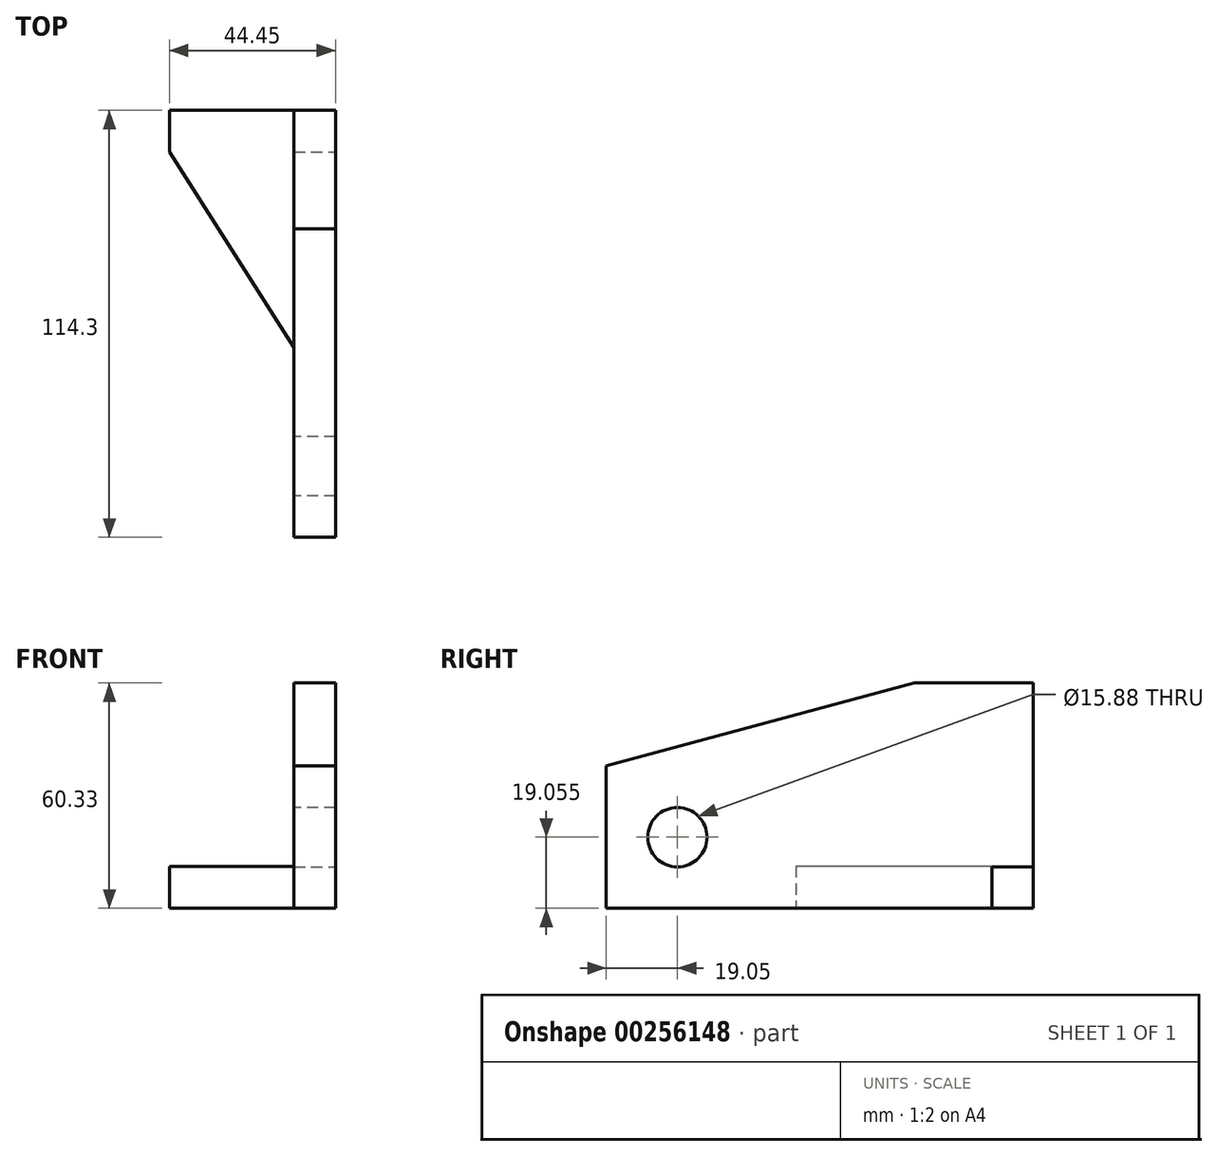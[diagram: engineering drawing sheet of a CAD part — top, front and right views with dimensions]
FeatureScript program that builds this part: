
annotation { "Feature Type Name" : "Feature", "Feature Type Description" : "" }
export const myFeature = defineFeature(function(context is Context, id is Id, definition is map)
    precondition{}
    {
        {
            var Q0;
            Q0=qCreatedBy(makeId("Front.planeOp"),FACE);
            var sketch = newSketch(context, id + "F0", { "sketchPlane" : qUnion([Q0])});
            skLineSegment(sketch, "E0.bottom", {"start": v(-5.09, -11.25) * mm, "end": v(-16.2, -11.25) * mm});
            skLineSegment(sketch, "E0.top", {"start": v(-5.09, 49.08) * mm, "end": v(-16.2, 49.08) * mm});
            skLineSegment(sketch, "E0.left", {"start": v(-5.09, -11.25) * mm, "end": v(-5.09, 49.08) * mm});
            skLineSegment(sketch, "E0.right", {"start": v(-16.2, -11.25) * mm, "end": v(-16.2, 49.08) * mm});
            skLineSegment(sketch, "E1", {"start": v(-16.2, -11.25) * mm, "end": v(-16.2, 39.55) * mm});
            skLineSegment(sketch, "E2", {"start": v(-5.09, -11.25) * mm, "end": v(-49.54, -11.25) * mm});
            skPoint(sketch, "E2.endSnap0", {"position": v(-10.64, -11.25) * mm});
            skLineSegment(sketch, "E3", {"start": v(-49.54, -11.25) * mm, "end": v(-49.54, 10.98) * mm});
            skLineSegment(sketch, "E4", {"start": v(-16.2, 39.55) * mm, "end": v(-33.04, 39.55) * mm});
            skLineSegment(sketch, "E5", {"start": v(-49.54, 10.98) * mm, "end": v(-33.04, 39.55) * mm});
            skPoint(sketch, "E6.end.orphan", {"position": v(-49.54, 39.55) * mm});
            skPoint(sketch, "E7.oppositeSnap0", {"position": v(-49.54, -0.13) * mm});
            skLineSegment(sketch, "E7.bottom", {"start": v(-49.54, -11.25) * mm, "end": v(-5.09, -11.25) * mm});
            skLineSegment(sketch, "E7.top", {"start": v(-49.54, -0.13) * mm, "end": v(-5.09, -0.13) * mm});
            skLineSegment(sketch, "E7.left", {"start": v(-49.54, -11.25) * mm, "end": v(-49.54, -0.13) * mm});
            skLineSegment(sketch, "E7.right", {"start": v(-5.09, -11.25) * mm, "end": v(-5.09, -0.13) * mm});
            skSolve(sketch);
        }
        {
            var Q0;
            {var subQ1=sQuery(id+"F0.wireOp",EDGE,"E3");Q0=makeQuery(id+"F0.imprint","IMPRINT",FACE,{"disambiguationData":[TD([[makeQuery(id+"F0.imprint","IMPRINT",EDGE,{"derivedFrom":subQ1}),-1.0]])]});}
            var Q1;
            {var subQ5=sQuery(id+"F0.wireOp",EDGE,"E7.left");Q1=makeQuery(id+"F0.imprint","IMPRINT",FACE,{"disambiguationData":[TD([[makeQuery(id+"F0.imprint","IMPRINT",EDGE,{"derivedFrom":subQ5}),-1.0]])]});}
            var Q2;
            {var subQ5=sQuery(id+"F0.wireOp",EDGE,"E7.right");Q2=makeQuery(id+"F0.imprint","IMPRINT",FACE,{"disambiguationData":[TD([[makeQuery(id+"F0.imprint","IMPRINT",EDGE,{"derivedFrom":subQ5}),1.0]])]});}
            var Q3;
            Q3=makeQuery(id+"F0.imprint","IMPRINT",FACE,{"disambiguationData":[TD([[makeQuery(id+"F0.imprint","IMPRINT",EDGE,{"derivedFrom":sQuery(id+"F0.wireOp",EDGE,"E0.top")}),1.0]])]});
            extrude(context, id + "F1", {"entities" : qUnion([Q0, Q1, Q2, Q3]), "depth" : 11.1 * mm});
        }
        {
            var Q0;
            Q0=makeQuery(id+"F1.opExtrude","CAP_FACE",FACE,{"disambiguationData":[OSD([sQuery(id+"F0.wireOp",EDGE,"E0.top"),sQuery(id+"F0.wireOp",EDGE,"E0.left"),sQuery(id+"F0.wireOp",EDGE,"E0.right"),sQuery(id+"F0.wireOp",EDGE,"E3"),sQuery(id+"F0.wireOp",EDGE,"E4"),sQuery(id+"F0.wireOp",EDGE,"E5"),sQuery(id+"F0.wireOp",EDGE,"E7.bottom"),sQuery(id+"F0.wireOp",EDGE,"E7.left"),sQuery(id+"F0.wireOp",EDGE,"E7.right")])],"isStart":false});
            var sketch = newSketch(context, id + "F2", { "sketchPlane" : qUnion([Q0])});
            skLineSegment(sketch, "E8", {"start": v(-16.2, 49.08) * mm, "end": v(-16.2, -11.25) * mm});
            skLineSegment(sketch, "E9", {"start": v(-16.2, 49.08) * mm, "end": v(-5.09, 49.08) * mm});
            skLineSegment(sketch, "E10", {"start": v(-5.09, 49.08) * mm, "end": v(-5.09, -11.25) * mm});
            skLineSegment(sketch, "E11", {"start": v(-16.2, -11.25) * mm, "end": v(-5.09, -11.25) * mm});
            skSolve(sketch);
        }
        {
            var Q0;
            Q0 = qSketchRegion(id + "F2", true);
            extrude(context, id + "F3", {"entities" : qUnion([Q0]), "operationType" : NewBodyOperationType.ADD, "depth" : 103.19 * mm});
        }
        {
            var Q0;
            Q0=makeQuery(id+"F3.boolean.opBoolean","MERGE",FACE,{"derivedFrom":[makeQuery(id+"F1.opExtrude","SWEPT_FACE",FACE,{"disambiguationData":[OSD([sQuery(id+"F0.wireOp",EDGE,"E0.right")])]}),makeQuery(id+"F3.opExtrude","SWEPT_FACE",FACE,{"disambiguationData":[OSD([sQuery(id+"F2.wireOp",EDGE,"E8")])]})]});
            var sketch = newSketch(context, id + "F4", { "sketchPlane" : qUnion([Q0])});
            skLineSegment(sketch, "E12", {"start": v(0, 49.08) * mm, "end": v(31.75, 49.08) * mm});
            skLineSegment(sketch, "E13", {"start": v(0, 49.08) * mm, "end": v(114.3, 49.08) * mm});
            skLineSegment(sketch, "E14", {"start": v(0, 49.08) * mm, "end": v(0, -11.25) * mm});
            skLineSegment(sketch, "E15", {"start": v(114.3, -11.25) * mm, "end": v(114.3, 49.08) * mm});
            skLineSegment(sketch, "E16", {"start": v(31.75, 49.08) * mm, "end": v(114.3, 26.96) * mm});
            skLineSegment(sketch, "E17", {"start": v(114.3, -11.25) * mm, "end": v(95.25, -11.25) * mm});
            skLineSegment(sketch, "E18", {"start": v(95.25, -11.25) * mm, "end": v(95.25, 7.8) * mm});
            skCircle(sketch, "E19", {"center": v(95.25, 7.8) * mm, "radius": 7.94 * mm});
            skSolve(sketch);
        }
        {
            var Q0;
            Q0=makeQuery(id+"F3.boolean.opBoolean","MERGE",FACE,{"derivedFrom":[makeQuery(id+"F1.opExtrude","SWEPT_FACE",FACE,{"disambiguationData":[OSD([sQuery(id+"F0.wireOp",EDGE,"E0.right")])]}),makeQuery(id+"F3.opExtrude","SWEPT_FACE",FACE,{"disambiguationData":[OSD([sQuery(id+"F2.wireOp",EDGE,"E8")])]})]});
            var sketch = newSketch(context, id + "F5", { "sketchPlane" : qUnion([Q0])});
            skLineSegment(sketch, "E20", {"start": v(0, 0) * mm, "end": v(63.5, 0) * mm});
            skLineSegment(sketch, "E21", {"start": v(63.5, 0) * mm, "end": v(63.5, -11.25) * mm});
            skPoint(sketch, "E22", {"position": v(63.5, -11.25) * mm});
            skSolve(sketch);
        }
        {
            var Q0;
            {var subQ3=sQuery(id+"F4.wireOp",EDGE,"E16");Q0=makeQuery(id+"F4.imprint","IMPRINT",FACE,{"disambiguationData":[TD([[makeQuery(id+"F4.imprint","IMPRINT",EDGE,{"derivedFrom":subQ3}),1.0]])]});}
            var Q1;
            Q1=makeQuery(id+"F4.imprint","IMPRINT",FACE,{"disambiguationData":[TD([[makeQuery(id+"F4.imprint","IMPRINT",EDGE,{"derivedFrom":sQuery(id+"F4.wireOp",EDGE,"E19")}),1.0]])]});
            extrude(context, id + "F6", {"entities" : qUnion([Q0, Q1]), "operationType" : NewBodyOperationType.REMOVE, "oppositeDirection" : true, "depth" : 25.4 * mm});
        }
        {
            var Q0;
            {var subQ0=sQuery(id+"F5.wireOp",EDGE,"E21");Q0=makeQuery(id+"F5.imprint","IMPRINT",FACE,{"disambiguationData":[TD([[makeQuery(id+"F5.imprint","IMPRINT",EDGE,{"derivedFrom":subQ0}),-1.0]])]});}
            extrude(context, id + "F7", {"entities" : qUnion([Q0]), "operationType" : NewBodyOperationType.ADD, "depth" : 33.34 * mm});
        }
        {
            var Q0;
            Q0=makeQuery(id+"F7.opExtrude","SWEPT_FACE",FACE,{"disambiguationData":[OSD([sQuery(id+"F5.wireOp",EDGE,"E20")])]});
            var sketch = newSketch(context, id + "F8", { "sketchPlane" : qUnion([Q0])});
            skLineSegment(sketch, "E23", {"start": v(-49.54, -11.11) * mm, "end": v(-16.2, -63.5) * mm});
            skSolve(sketch);
        }
        {
            var Q0;
            Q0=makeQuery(id+"F8.imprint","IMPRINT",FACE,{"disambiguationData":[TD([[makeQuery(id+"F8.imprint","IMPRINT",EDGE,{"derivedFrom":sQuery(id+"F8.wireOp",EDGE,"E23")}),-1.0]])]});
            extrude(context, id + "F9", {"entities" : qUnion([Q0]), "operationType" : NewBodyOperationType.REMOVE, "oppositeDirection" : true, "depth" : 25.4 * mm});
        }
    });
